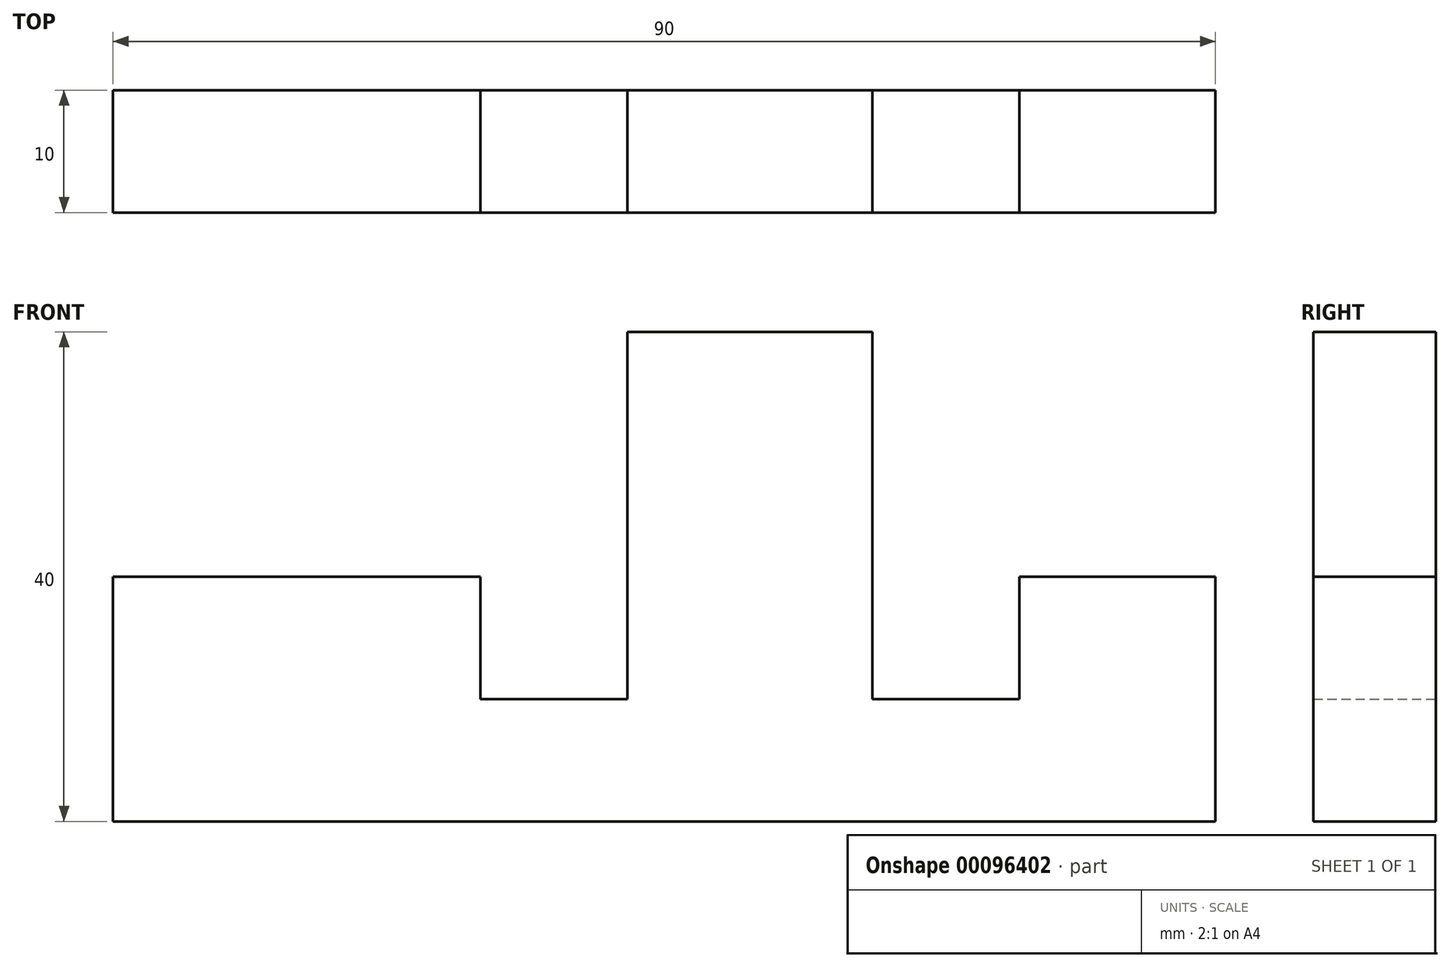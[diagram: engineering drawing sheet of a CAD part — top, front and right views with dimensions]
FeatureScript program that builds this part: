
annotation { "Feature Type Name" : "Feature", "Feature Type Description" : "" }
export const myFeature = defineFeature(function(context is Context, id is Id, definition is map)
    precondition{}
    {
        {
            var Q0;
            Q0=qCreatedBy(makeId("Front.planeOp"),FACE);
            var sketch = newSketch(context, id + "F0", { "sketchPlane" : qUnion([Q0])});
            skLineSegment(sketch, "E0", {"start": v(0, 0) * mm, "end": v(90, 0) * mm});
            skLineSegment(sketch, "E1", {"start": v(90, 0) * mm, "end": v(90, 20) * mm});
            skLineSegment(sketch, "E2", {"start": v(90, 20) * mm, "end": v(74, 20) * mm});
            skLineSegment(sketch, "E3", {"start": v(74, 20) * mm, "end": v(74, 10) * mm});
            skLineSegment(sketch, "E4", {"start": v(74, 10) * mm, "end": v(62, 10) * mm});
            skLineSegment(sketch, "E5", {"start": v(62, 10) * mm, "end": v(62, 40) * mm});
            skLineSegment(sketch, "E6", {"start": v(62, 40) * mm, "end": v(42, 40) * mm});
            skLineSegment(sketch, "E7", {"start": v(42, 40) * mm, "end": v(42, 10) * mm});
            skLineSegment(sketch, "E8", {"start": v(42, 10) * mm, "end": v(30, 10) * mm});
            skLineSegment(sketch, "E9", {"start": v(30, 10) * mm, "end": v(30, 20) * mm});
            skLineSegment(sketch, "E10", {"start": v(30, 20) * mm, "end": v(0, 20) * mm});
            skLineSegment(sketch, "E11", {"start": v(0, 20) * mm, "end": v(0, 0) * mm});
            skSolve(sketch);
        }
        {
            var Q0;
            Q0=makeQuery(id+"F0.imprint","IMPRINT",FACE,{"disambiguationData":[TD([[makeQuery(id+"F0.imprint","IMPRINT",EDGE,{"derivedFrom":sQuery(id+"F0.wireOp",EDGE,"E0")}),1.0]])]});
            extrude(context, id + "F1", {"entities" : qUnion([Q0]), "depth" : 10 * mm});
        }
    });
